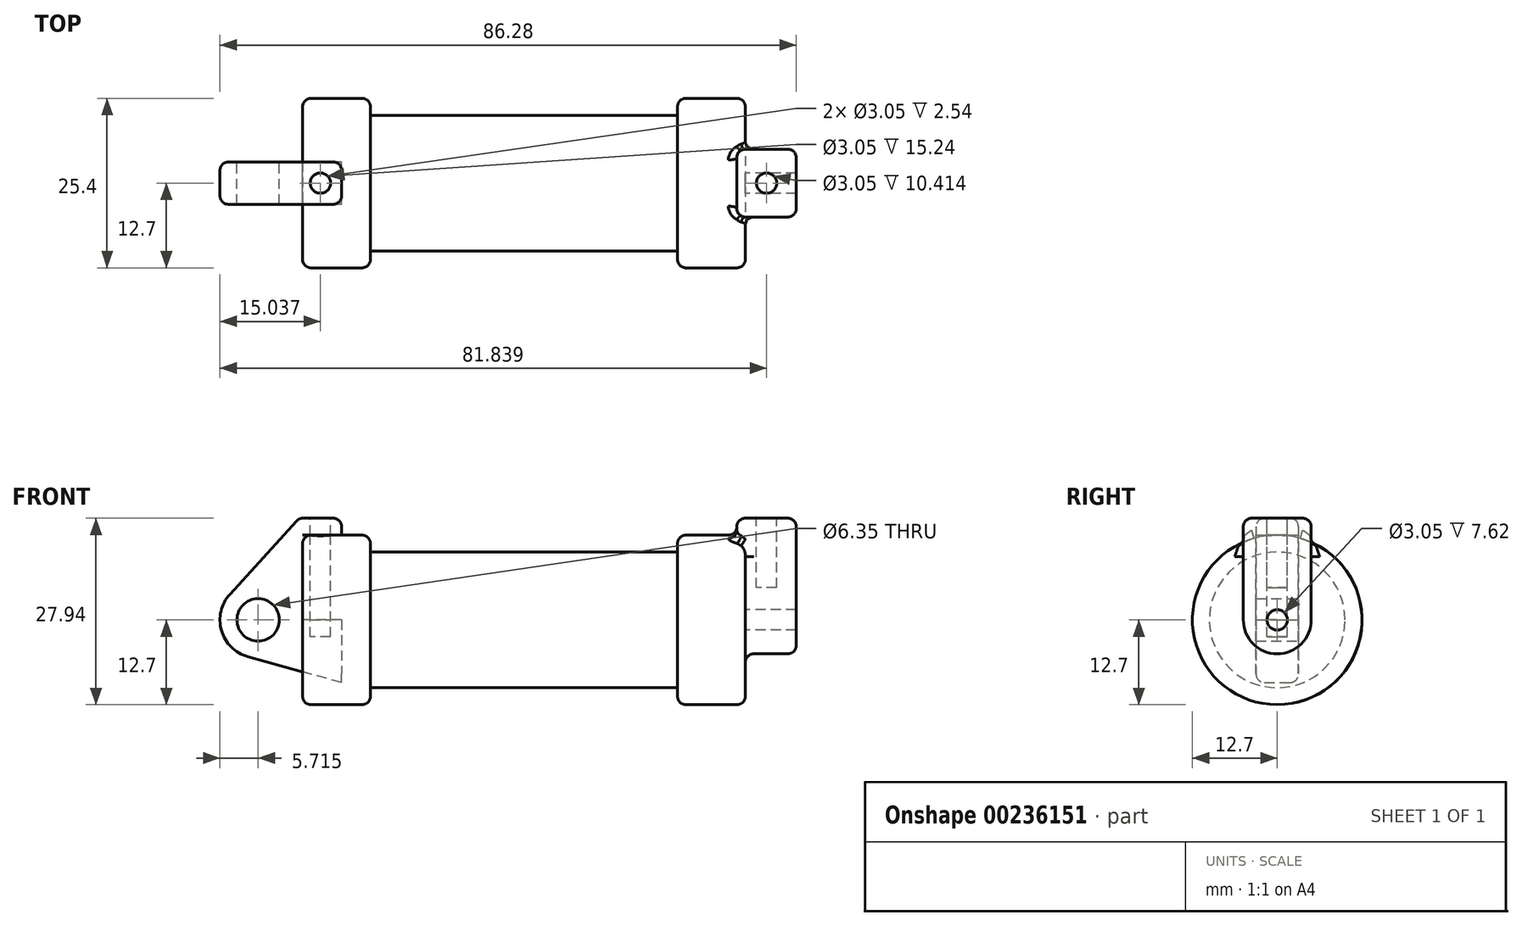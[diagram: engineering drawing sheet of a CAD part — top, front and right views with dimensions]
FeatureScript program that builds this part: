
annotation { "Feature Type Name" : "Feature", "Feature Type Description" : "" }
export const myFeature = defineFeature(function(context is Context, id is Id, definition is map)
    precondition{}
    {
        {
            var Q0;
            Q0=qCreatedBy(makeId("Front.planeOp"),FACE);
            var sketch = newSketch(context, id + "F0", { "sketchPlane" : qUnion([Q0])});
            skLineSegment(sketch, "E0", {"start": v(0, 0) * mm, "end": v(0, 12.7) * mm});
            skLineSegment(sketch, "E1", {"start": v(0, 12.7) * mm, "end": v(10.16, 12.7) * mm});
            skLineSegment(sketch, "E2", {"start": v(10.16, 12.7) * mm, "end": v(10.16, 10.16) * mm});
            skLineSegment(sketch, "E3", {"start": v(10.16, 10.16) * mm, "end": v(56.13, 10.16) * mm});
            skLineSegment(sketch, "E4", {"start": v(56.13, 10.16) * mm, "end": v(56.13, 12.7) * mm});
            skLineSegment(sketch, "E5", {"start": v(56.13, 12.7) * mm, "end": v(66.3, 12.7) * mm});
            skLineSegment(sketch, "E6", {"start": v(66.3, 12.7) * mm, "end": v(66.3, 0) * mm});
            skLineSegment(sketch, "E7", {"start": v(66.3, 0) * mm, "end": v(0, 0) * mm});
            skLineSegment(sketch, "E8", {"start": v(5.84, 15.24) * mm, "end": v(-0.5, 15.24) * mm});
            skLineSegment(sketch, "E9", {"start": v(-0.5, 15.24) * mm, "end": v(-10.88, 3.85) * mm});
            skLineSegment(sketch, "E10", {"start": v(0, 0) * mm, "end": v(-6.65, 0) * mm});
            skCircle(sketch, "E11", {"center": v(-6.65, 0) * mm, "radius": 5.72 * mm});
            skCircle(sketch, "E12", {"center": v(-6.65, 0) * mm, "radius": 3.18 * mm});
            skLineSegment(sketch, "E13", {"start": v(5.84, 15.24) * mm, "end": v(5.84, -9.4) * mm});
            skLineSegment(sketch, "E14", {"start": v(5.84, -9.4) * mm, "end": v(-8.18, -5.5) * mm});
            skSolve(sketch);
        }
        {
            var Q0;
            {var subQ0=sQuery(id+"F0.wireOp",EDGE,"E2");Q0=makeQuery(id+"F0.imprint","IMPRINT",FACE,{"disambiguationData":[TD([[makeQuery(id+"F0.imprint","IMPRINT",EDGE,{"derivedFrom":subQ0}),-1.0]])]});}
            var Q1;
            {var subQ0=sQuery(id+"F0.wireOp",EDGE,"E0");Q1=makeQuery(id+"F0.imprint","IMPRINT",FACE,{"disambiguationData":[TD([[makeQuery(id+"F0.imprint","IMPRINT",EDGE,{"derivedFrom":subQ0}),-1.0]])]});}
            var Q2;
            Q2=sQuery(id+"F0.wireOp",EDGE,"E7");
            revolve(context, id + "F1", {"entities" : qUnion([Q0, Q1]), "axis" : qUnion([Q2]), "revolveType" : RevolveType.FULL});
        }
        {
            var Q0;
            {var subQ3=sQuery(id+"F0.wireOp",EDGE,"E0");Q0=makeQuery(id+"F0.imprint","IMPRINT",FACE,{"disambiguationData":[TD([[makeQuery(id+"F0.imprint","IMPRINT",EDGE,{"derivedFrom":subQ3}),1.0]])]});}
            var Q1;
            {var subQ4=sQuery(id+"F0.wireOp",EDGE,"E12");Q1=makeQuery(id+"F0.imprint","IMPRINT",FACE,{"disambiguationData":[TD([[makeQuery(id+"F0.imprint","IMPRINT",EDGE,{"derivedFrom":subQ4}),-1.0]])]});}
            var Q2;
            {var subQ0=sQuery(id+"F0.wireOp",EDGE,"E14");Q2=makeQuery(id+"F0.imprint","IMPRINT",FACE,{"disambiguationData":[TD([[makeQuery(id+"F0.imprint","IMPRINT",EDGE,{"derivedFrom":subQ0}),-1.0]])]});}
            extrude(context, id + "F2", {"entities" : qUnion([Q0, Q1, Q2]), "endBound" : BoundingType.SYMMETRIC, "depth" : 6.35 * mm});
        }
        {
            var Q0;
            Q0=makeQuery(id+"F1.opRevolve","SWEPT_FACE",FACE,{"disambiguationData":[OSD([sQuery(id+"F0.wireOp",EDGE,"E6")])]});
            var sketch = newSketch(context, id + "F3", { "sketchPlane" : qUnion([Q0])});
            skCircle(sketch, "E15", {"center": v(0, 0) * mm, "radius": 1.52 * mm});
            skCircle(sketch, "E16", {"center": v(0, 0) * mm, "radius": 5.08 * mm});
            skLineSegment(sketch, "E17", {"start": v(-5.08, 0) * mm, "end": v(-5.08, 15.3) * mm});
            skLineSegment(sketch, "E18", {"start": v(5.08, 0) * mm, "end": v(5.08, 15.24) * mm});
            skLineSegment(sketch, "E19", {"start": v(5.08, 15.24) * mm, "end": v(-5.08, 15.24) * mm});
            skSolve(sketch);
        }
        {
            var Q0;
            Q0 = qSketchRegion(id + "F3", true);
            extrude(context, id + "F4", {"entities" : qUnion([Q0]), "depth" : 7.62 * mm});
        }
        {
            var Q0;
            Q0 = qSketchRegion(id + "F3", true);
            extrude(context, id + "F5", {"entities" : qUnion([Q0]), "operationType" : NewBodyOperationType.ADD, "oppositeDirection" : true, "depth" : 1.27 * mm});
        }
        {
            var Q0;
            {var subQ0=sQuery(id+"F3.wireOp",EDGE,"E15");Q0=makeQuery(id+"F5.boolean.opBoolean","SPLIT",FACE,{"disambiguationData":[TD([makeQuery(id+"F4.opExtrude","SWEPT_FACE",FACE,{"disambiguationData":[OSD([subQ0])]})])],"derivedFrom":makeQuery(id+"F1.opRevolve","SWEPT_FACE",FACE,{"disambiguationData":[OSD([sQuery(id+"F0.wireOp",EDGE,"E6")])]})});}
            var Q1;
            Q1=makeQuery(id+"F1.opRevolve","SWEPT_FACE",FACE,{"disambiguationData":[OSD([sQuery(id+"F0.wireOp",EDGE,"E2")])]});
            extrude(context, id + "F6", {"entities" : qUnion([Q0]), "operationType" : NewBodyOperationType.ADD, "endBound" : BoundingType.UP_TO_SURFACE, "oppositeDirection" : true, "endBoundEntityFace" : qUnion([Q1]), "depth" : 25.4 * mm});
        }
        {
            var Q0;
            Q0=makeQuery(id+"F2.opExtrude","SWEPT_FACE",FACE,{"disambiguationData":[OSD([sQuery(id+"F0.wireOp",EDGE,"E8")])]});
            var sketch = newSketch(context, id + "F7", { "sketchPlane" : qUnion([Q0])});
            skLineSegment(sketch, "E20.0.0", {"start": v(5.84, 3.18) * mm, "end": v(-0.5, 3.18) * mm});
            skLineSegment(sketch, "E20.0.1", {"start": v(-0.5, 3.17) * mm, "end": v(-0.5, -3.18) * mm});
            skLineSegment(sketch, "E20.0.2", {"start": v(-0.5, -3.18) * mm, "end": v(5.84, -3.18) * mm});
            skLineSegment(sketch, "E20.0.3", {"start": v(5.84, -3.18) * mm, "end": v(5.84, 3.17) * mm});
            skCircle(sketch, "E21", {"center": v(2.67, 0) * mm, "radius": 1.52 * mm});
            skSolve(sketch);
        }
        {
            var Q0;
            Q0=makeQuery(id+"F7.imprint","IMPRINT",FACE,{"disambiguationData":[TD([[makeQuery(id+"F7.imprint","IMPRINT",EDGE,{"derivedFrom":sQuery(id+"F7.wireOp",EDGE,"E21")}),1.0]])]});
            var Q1;
            Q1=sQuery(id+"F7.wireOp",EDGE,"E21");
            extrude(context, id + "F8", {"entities" : qUnion([Q0]), "operationType" : NewBodyOperationType.REMOVE, "surfaceEntities" : qUnion([Q1]), "oppositeDirection" : true, "depth" : 17.78 * mm});
        }
        {
            var Q0;
            {var subQ0=sQuery(id+"F3.wireOp",EDGE,"E19");Q0=makeQuery(id+"F5.boolean.opBoolean","MERGE",FACE,{"derivedFrom":[makeQuery(id+"F4.opExtrude","SWEPT_FACE",FACE,{"disambiguationData":[OSD([subQ0])]}),makeQuery(id+"F5.opExtrude","SWEPT_FACE",FACE,{"disambiguationData":[OSD([subQ0])]})]});}
            var sketch = newSketch(context, id + "F9", { "sketchPlane" : qUnion([Q0])});
            skLineSegment(sketch, "E22.0.0", {"start": v(73.91, 5.08) * mm, "end": v(65.02, 5.08) * mm});
            skLineSegment(sketch, "E22.0.1", {"start": v(65.02, 5.08) * mm, "end": v(65.02, -5.08) * mm});
            skLineSegment(sketch, "E22.0.2", {"start": v(65.02, -5.08) * mm, "end": v(73.91, -5.08) * mm});
            skLineSegment(sketch, "E22.0.3", {"start": v(73.91, -5.08) * mm, "end": v(73.91, 5.08) * mm});
            skCircle(sketch, "E23", {"center": v(69.47, 0) * mm, "radius": 1.52 * mm});
            skSolve(sketch);
        }
        {
            var Q0;
            Q0=makeQuery(id+"F9.imprint","IMPRINT",FACE,{"disambiguationData":[TD([[makeQuery(id+"F9.imprint","IMPRINT",EDGE,{"derivedFrom":sQuery(id+"F9.wireOp",EDGE,"E23")}),1.0]])]});
            extrude(context, id + "F10", {"entities" : qUnion([Q0]), "operationType" : NewBodyOperationType.REMOVE, "oppositeDirection" : true, "depth" : 10.4 * mm});
        }
        {
            var Q0;
            Q0=makeQuery(id+"F1.opRevolve","SWEPT_EDGE",EDGE,{"disambiguationData":[OSD([sQuery(id+"F0.wireOp",EDGE,"E1"),sQuery(id+"F0.wireOp",EDGE,"E2")])]});
            var Q1;
            Q1=makeQuery(id+"F1.opRevolve","SWEPT_EDGE",EDGE,{"disambiguationData":[OSD([sQuery(id+"F0.wireOp",EDGE,"E4"),sQuery(id+"F0.wireOp",EDGE,"E5")])]});
            var Q2;
            Q2=makeQuery(id+"F1.opRevolve","SWEPT_EDGE",EDGE,{"disambiguationData":[OSD([sQuery(id+"F0.wireOp",EDGE,"E5"),sQuery(id+"F0.wireOp",EDGE,"E6")])]});
            var Q3;
            Q3=makeQuery(id+"F1.opRevolve","SWEPT_EDGE",EDGE,{"disambiguationData":[OSD([sQuery(id+"F0.wireOp",EDGE,"E0"),sQuery(id+"F0.wireOp",EDGE,"E1")])]});
            fillet(context, id + "F11", {"entities" : qUnion([Q0, Q1, Q2, Q3]), "radius" : 1.27 * mm, "tangentPropagation" : true, "allowEdgeOverflow" : false});
        }
        {
            var Q0;
            Q0=makeQuery(id+"F2.opExtrude","CAP_EDGE",EDGE,{"disambiguationData":[OSD([sQuery(id+"F0.wireOp",EDGE,"E8")])],"isStart":false});
            var Q1;
            Q1=makeQuery(id+"F2.opExtrude","CAP_EDGE",EDGE,{"disambiguationData":[OSD([sQuery(id+"F0.wireOp",EDGE,"E8")])],"isStart":true});
            var Q2;
            Q2=makeQuery(id+"F2.opExtrude","SWEPT_EDGE",EDGE,{"disambiguationData":[OSD([sQuery(id+"F0.wireOp",EDGE,"E8"),sQuery(id+"F0.wireOp",EDGE,"E13")])]});
            var Q3;
            Q3=makeQuery(id+"F2.opExtrude","CAP_EDGE",EDGE,{"disambiguationData":[OSD([sQuery(id+"F0.wireOp",EDGE,"E9")])],"isStart":false});
            var Q4;
            Q4=makeQuery(id+"F2.opExtrude","CAP_EDGE",EDGE,{"disambiguationData":[OSD([sQuery(id+"F0.wireOp",EDGE,"E9")])],"isStart":true});
            var Q5;
            Q5=makeQuery(id+"F2.opExtrude","CAP_EDGE",EDGE,{"disambiguationData":[OSD([sQuery(id+"F0.wireOp",EDGE,"E11")])],"isStart":false});
            var Q6;
            Q6=makeQuery(id+"F2.opExtrude","CAP_EDGE",EDGE,{"disambiguationData":[OSD([sQuery(id+"F0.wireOp",EDGE,"E11")])],"isStart":true});
            var Q7;
            {var subQ0=sQuery(id+"F0.wireOp",EDGE,"E13");Q7=makeQuery(id+"F2.opExtrude","CAP_EDGE",EDGE,{"disambiguationData":[OSD([subQ0]),TDD([makeQuery(id+"F0.imprint","IMPRINT",EDGE,{"disambiguationData":[TD([[makeQuery(id+"F0.imprint","INTERSECT",VERTEX,{"derivedFrom":[sQuery(id+"F0.wireOp",EDGE,"E8"),subQ0]}),-1.0]])],"derivedFrom":subQ0})])],"isStart":true});}
            var Q8;
            Q8=makeQuery(id+"F2.opExtrude","CAP_EDGE",EDGE,{"disambiguationData":[OSD([sQuery(id+"F0.wireOp",EDGE,"E14")])],"isStart":true});
            var Q9;
            Q9=makeQuery(id+"F2.opExtrude","SWEPT_EDGE",EDGE,{"disambiguationData":[OSD([sQuery(id+"F0.wireOp",EDGE,"E8"),sQuery(id+"F0.wireOp",EDGE,"E9")])]});
            var Q10;
            Q10=makeQuery(id+"F2.opExtrude","SWEPT_EDGE",EDGE,{"disambiguationData":[OSD([sQuery(id+"F0.wireOp",EDGE,"E9"),sQuery(id+"F0.wireOp",EDGE,"E11")])]});
            var Q11;
            Q11=makeQuery(id+"F2.opExtrude","SWEPT_EDGE",EDGE,{"disambiguationData":[OSD([sQuery(id+"F0.wireOp",EDGE,"E11"),sQuery(id+"F0.wireOp",EDGE,"E14")])]});
            var Q12;
            Q12=makeQuery(id+"F2.opExtrude","CAP_EDGE",EDGE,{"disambiguationData":[OSD([sQuery(id+"F0.wireOp",EDGE,"E14")])],"isStart":false});
            var Q13;
            {var subQ0=sQuery(id+"F0.wireOp",EDGE,"E13");Q13=makeQuery(id+"F2.opExtrude","CAP_EDGE",EDGE,{"disambiguationData":[OSD([subQ0]),TDD([makeQuery(id+"F0.imprint","IMPRINT",EDGE,{"disambiguationData":[TD([[makeQuery(id+"F0.imprint","INTERSECT",VERTEX,{"derivedFrom":[sQuery(id+"F0.wireOp",EDGE,"E8"),subQ0]}),-1.0]])],"derivedFrom":subQ0})])],"isStart":false});}
            fillet(context, id + "F12", {"entities" : qUnion([Q0, Q1, Q2, Q3, Q4, Q5, Q6, Q7, Q8, Q9, Q10, Q11, Q12, Q13]), "radius" : 1.27 * mm, "tangentPropagation" : true, "allowEdgeOverflow" : false});
        }
        {
            var Q0;
            Q0=makeQuery(id+"F5.opExtrude","CAP_EDGE",EDGE,{"disambiguationData":[OSD([sQuery(id+"F3.wireOp",EDGE,"E19")])],"isStart":false});
            var Q1;
            {var subQ0=sQuery(id+"F3.wireOp",EDGE,"E19");var subQ1=sQuery(id+"F3.wireOp",EDGE,"E17");Q1=makeQuery(id+"F5.boolean.opBoolean","MERGE",EDGE,{"derivedFrom":[makeQuery(id+"F4.opExtrude","SWEPT_EDGE",EDGE,{"disambiguationData":[OSD([subQ1,subQ0])]}),makeQuery(id+"F5.opExtrude","SWEPT_EDGE",EDGE,{"disambiguationData":[OSD([subQ1,subQ0])]})]});}
            var Q2;
            Q2=makeQuery(id+"F4.opExtrude","CAP_EDGE",EDGE,{"disambiguationData":[OSD([sQuery(id+"F3.wireOp",EDGE,"E19")])],"isStart":false});
            var Q3;
            {var subQ0=sQuery(id+"F3.wireOp",EDGE,"E19");var subQ1=sQuery(id+"F3.wireOp",EDGE,"E18");Q3=makeQuery(id+"F5.boolean.opBoolean","MERGE",EDGE,{"derivedFrom":[makeQuery(id+"F4.opExtrude","SWEPT_EDGE",EDGE,{"disambiguationData":[OSD([subQ1,subQ0])]}),makeQuery(id+"F5.opExtrude","SWEPT_EDGE",EDGE,{"disambiguationData":[OSD([subQ1,subQ0])]})]});}
            var Q4;
            Q4=makeQuery(id+"F4.opExtrude","CAP_EDGE",EDGE,{"disambiguationData":[OSD([sQuery(id+"F3.wireOp",EDGE,"E17")])],"isStart":false});
            var Q5;
            Q5=makeQuery(id+"F4.opExtrude","CAP_EDGE",EDGE,{"disambiguationData":[OSD([sQuery(id+"F3.wireOp",EDGE,"E18")])],"isStart":false});
            var Q6;
            Q6=makeQuery(id+"F4.opExtrude","CAP_EDGE",EDGE,{"disambiguationData":[OSD([sQuery(id+"F3.wireOp",EDGE,"E16")])],"isStart":false});
            var Q7;
            {var subQ0=sQuery(id+"F3.wireOp",EDGE,"E17");var subQ1=sQuery(id+"F3.wireOp",EDGE,"E16");Q7=makeQuery(id+"F5.boolean.opBoolean","MERGE",EDGE,{"derivedFrom":[makeQuery(id+"F4.opExtrude","SWEPT_EDGE",EDGE,{"disambiguationData":[OSD([subQ1,subQ0])]}),makeQuery(id+"F5.opExtrude","SWEPT_EDGE",EDGE,{"disambiguationData":[OSD([subQ1,subQ0])]})]});}
            var Q8;
            {var subQ0=sQuery(id+"F3.wireOp",EDGE,"E18");var subQ1=sQuery(id+"F3.wireOp",EDGE,"E16");Q8=makeQuery(id+"F5.boolean.opBoolean","MERGE",EDGE,{"derivedFrom":[makeQuery(id+"F4.opExtrude","SWEPT_EDGE",EDGE,{"disambiguationData":[OSD([subQ1,subQ0])]}),makeQuery(id+"F5.opExtrude","SWEPT_EDGE",EDGE,{"disambiguationData":[OSD([subQ1,subQ0])]})]});}
            var Q9;
            Q9=makeQuery(id+"F5.boolean.opBoolean","INTERSECT",EDGE,{"derivedFrom":[makeQuery(id+"F1.opRevolve","SWEPT_FACE",FACE,{"disambiguationData":[OSD([sQuery(id+"F0.wireOp",EDGE,"E6")])]}),makeQuery(id+"F5.opExtrude","SWEPT_FACE",FACE,{"disambiguationData":[OSD([sQuery(id+"F3.wireOp",EDGE,"E16")])]})]});
            var Q10;
            Q10=makeQuery(id+"F5.boolean.opBoolean","INTERSECT",EDGE,{"derivedFrom":[makeQuery(id+"F1.opRevolve","SWEPT_FACE",FACE,{"disambiguationData":[OSD([sQuery(id+"F0.wireOp",EDGE,"E6")])]}),makeQuery(id+"F5.opExtrude","SWEPT_FACE",FACE,{"disambiguationData":[OSD([sQuery(id+"F3.wireOp",EDGE,"E17")])]})]});
            var Q11;
            Q11=makeQuery(id+"F5.opExtrude","CAP_EDGE",EDGE,{"disambiguationData":[OSD([sQuery(id+"F3.wireOp",EDGE,"E18")])],"isStart":false});
            var Q12;
            {var subQ0=sQuery(id+"F0.wireOp",EDGE,"E5");Q12=makeQuery(id+"F11.opFillet","BLEND_EDGE",EDGE,{"blendedFrom":[makeQuery(id+"F1.opRevolve","SWEPT_EDGE",EDGE,{"disambiguationData":[OSD([subQ0,sQuery(id+"F0.wireOp",EDGE,"E6")])]}),makeQuery(id+"F1.opRevolve","SWEPT_FACE",FACE,{"disambiguationData":[OSD([subQ0])]})],"blendedInto":[makeQuery(id+"F1.opRevolve","SWEPT_FACE",FACE,{"disambiguationData":[OSD([subQ0])]})]});}
            var Q13;
            Q13=makeQuery(id+"F5.boolean.opBoolean","INTERSECT",EDGE,{"derivedFrom":[makeQuery(id+"F1.opRevolve","SWEPT_FACE",FACE,{"disambiguationData":[OSD([sQuery(id+"F0.wireOp",EDGE,"E6")])]}),makeQuery(id+"F5.opExtrude","SWEPT_FACE",FACE,{"disambiguationData":[OSD([sQuery(id+"F3.wireOp",EDGE,"E18")])]})]});
            var Q14;
            Q14=makeQuery(id+"F5.opExtrude","CAP_EDGE",EDGE,{"disambiguationData":[OSD([sQuery(id+"F3.wireOp",EDGE,"E17")])],"isStart":false});
            var Q15;
            {var subQ0=sQuery(id+"F3.wireOp",EDGE,"E18");Q15=makeQuery(id+"F11.opFillet","BLEND_EDGE",EDGE,{"blendedFrom":[makeQuery(id+"F1.opRevolve","SWEPT_EDGE",EDGE,{"disambiguationData":[OSD([sQuery(id+"F0.wireOp",EDGE,"E5"),sQuery(id+"F0.wireOp",EDGE,"E6")])]}),makeQuery(id+"F5.boolean.opBoolean","MERGE",FACE,{"derivedFrom":[makeQuery(id+"F4.opExtrude","SWEPT_FACE",FACE,{"disambiguationData":[OSD([subQ0])]}),makeQuery(id+"F5.opExtrude","SWEPT_FACE",FACE,{"disambiguationData":[OSD([subQ0])]})]})],"blendedInto":[makeQuery(id+"F5.boolean.opBoolean","MERGE",FACE,{"derivedFrom":[makeQuery(id+"F4.opExtrude","SWEPT_FACE",FACE,{"disambiguationData":[OSD([subQ0])]}),makeQuery(id+"F5.opExtrude","SWEPT_FACE",FACE,{"disambiguationData":[OSD([subQ0])]})]})]});}
            var Q16;
            {var subQ0=sQuery(id+"F3.wireOp",EDGE,"E17");Q16=makeQuery(id+"F11.opFillet","BLEND_EDGE",EDGE,{"blendedFrom":[makeQuery(id+"F1.opRevolve","SWEPT_EDGE",EDGE,{"disambiguationData":[OSD([sQuery(id+"F0.wireOp",EDGE,"E5"),sQuery(id+"F0.wireOp",EDGE,"E6")])]}),makeQuery(id+"F5.boolean.opBoolean","MERGE",FACE,{"derivedFrom":[makeQuery(id+"F4.opExtrude","SWEPT_FACE",FACE,{"disambiguationData":[OSD([subQ0])]}),makeQuery(id+"F5.opExtrude","SWEPT_FACE",FACE,{"disambiguationData":[OSD([subQ0])]})]})],"blendedInto":[makeQuery(id+"F5.boolean.opBoolean","MERGE",FACE,{"derivedFrom":[makeQuery(id+"F4.opExtrude","SWEPT_FACE",FACE,{"disambiguationData":[OSD([subQ0])]}),makeQuery(id+"F5.opExtrude","SWEPT_FACE",FACE,{"disambiguationData":[OSD([subQ0])]})]})]});}
            var Q17;
            Q17=makeQuery(id+"F5.boolean.opBoolean","INTERSECT",EDGE,{"derivedFrom":[makeQuery(id+"F1.opRevolve","SWEPT_FACE",FACE,{"disambiguationData":[OSD([sQuery(id+"F0.wireOp",EDGE,"E5")])]}),makeQuery(id+"F5.opExtrude","CAP_FACE",FACE,{"disambiguationData":[OSD([sQuery(id+"F3.wireOp",EDGE,"E15"),sQuery(id+"F3.wireOp",EDGE,"E16"),sQuery(id+"F3.wireOp",EDGE,"E17"),sQuery(id+"F3.wireOp",EDGE,"E18"),sQuery(id+"F3.wireOp",EDGE,"E19")])],"isStart":false})]});
            fillet(context, id + "F13", {"entities" : qUnion([Q0, Q1, Q2, Q3, Q4, Q5, Q6, Q7, Q8, Q9, Q10, Q11, Q12, Q13, Q14, Q15, Q16, Q17]), "radius" : 1.27 * mm, "tangentPropagation" : true, "allowEdgeOverflow" : false});
        }
    });
